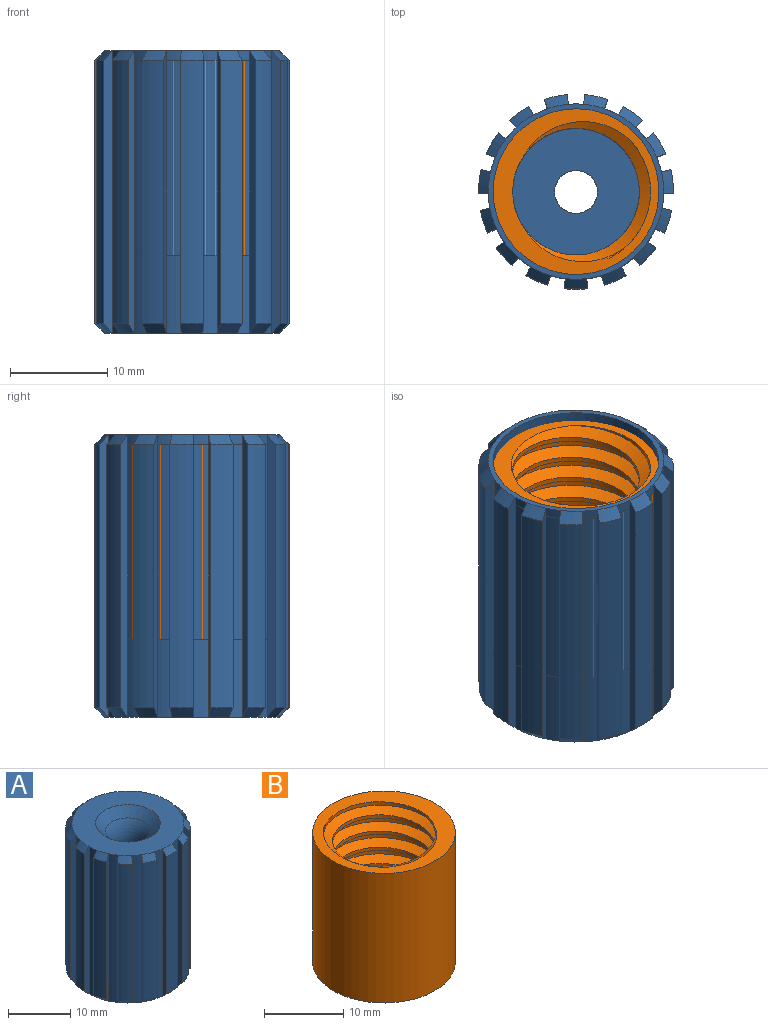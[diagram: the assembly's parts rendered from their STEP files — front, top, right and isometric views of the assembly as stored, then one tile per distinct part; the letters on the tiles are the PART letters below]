
ASSEMBLY  parts=2 mates=1
PART A: 97 faces, bbox 20x20x29 mm
  f0: cylinder r=10mm len=27mm, axis (0,0,-1), area 66mm2, adj f38,f62,f75,f84
  f1: cylinder r=10mm len=27mm, axis (0,0,-1), area 66mm2, adj f59,f64,f76,f83
  f2: cylinder r=10mm len=27mm, axis (0,0,-1), area 66mm2, adj f56,f61,f77,f82
  f3: cylinder r=10mm len=27mm, axis (0,0,-1), area 66mm2, adj f53,f58,f78,f81
  f4: cylinder r=10mm len=27mm, axis (0,0,-1), area 66mm2, adj f50,f55,f79,f80
  f5: cylinder r=10mm len=27mm, axis (0,0,-1), area 66mm2, adj f47,f52,f65,f94
  f6: cylinder r=10mm len=27mm, axis (0,0,-1), area 66mm2, adj f44,f49,f66,f93
  f7: cylinder r=10mm len=27mm, axis (0,0,-1), area 66mm2, adj f41,f46,f67,f92
  f8: cylinder r=10mm len=27mm, axis (0,0,-1), area 66mm2, adj f32,f39,f74,f85
  f9: cylinder r=10mm len=27mm, axis (0,0,-1), area 66mm2, adj f23,f36,f72,f87
  f10: cylinder r=10mm len=27mm, axis (0,0,-1), area 66mm2, adj f33,f35,f73,f86
  f11: cylinder r=10mm len=27mm, axis (0,0,-1), area 66mm2, adj f22,f30,f69,f90
  f12: cylinder r=10mm len=27mm, axis (0,0,-1), area 66mm2, adj f27,f29,f70,f89
  f13: cylinder r=10mm len=27mm, axis (0,0,-1), area 66mm2, adj f24,f26,f71,f88
  f14: plane 18x18mm, normal (0,0,1), area 169.5mm2, adj f21,f25,f28,f31,f34,f37,f40,f42
  f15: plane 18x18mm, normal (0,0,-1), area 27.5mm2, adj f19,f21,f25,f28,f31,f34,f37,f40
  f16: plane 17x17mm, normal (0,0,-1), area 211.8mm2, adj f18,f19
  f17: cylinder r=10mm len=27mm, axis (0,0,-1), area 66mm2, adj f20,f43,f68,f91
  f18: cylinder r=2.2mm len=4.4mm, axis (0,0,-1), area 40.5mm2, adj f16,f96
  f19: cylinder r=8.5mm len=21mm, axis (0,0,1), area 1121.5mm2, adj f15,f16
  f20: plane 29x1mm, normal (1,0.09,0), area 28mm2, adj f17,f21,f68,f91
  f21: cylinder r=9mm len=29mm, axis (0,0,1), area 45.6mm2, adj f14,f15,f20,f22
  f22: plane 29x1mm, normal (-1,0.09,0), area 28mm2, adj f11,f21,f69,f90
  f23: plane 29x0.97mm, normal (-0.22,0.97,0), area 28mm2, adj f9,f25,f72,f87
  f24: plane 29x0.92mm, normal (0.39,-0.92,0), area 28mm2, adj f13,f25,f71,f88
  f25: cylinder r=9mm len=29mm, axis (0,0,1), area 45.6mm2, adj f14,f15,f23,f24
  f26: plane 29x0.8mm, normal (-0.6,0.8,0), area 28mm2, adj f13,f28,f71,f88
  f27: plane 29x0.73mm, normal (0.73,-0.68,0), area 28mm2, adj f12,f28,f70,f89
  f28: cylinder r=9mm len=29mm, axis (0,0,1), area 45.6mm2, adj f14,f15,f26,f27
  f29: plane 29x0.87mm, normal (-0.87,0.48,0), area 28mm2, adj f12,f31,f70,f89
  f30: plane 29x0.95mm, normal (0.95,-0.33,0), area 28mm2, adj f11,f31,f69,f90
  f31: cylinder r=9mm len=29mm, axis (0,0,1), area 45.6mm2, adj f14,f15,f29,f30
  f32: plane 29x0.82mm, normal (0.57,0.82,0), area 28mm2, adj f8,f34,f74,f85
  f33: plane 29x0.91mm, normal (-0.42,-0.91,0), area 28mm2, adj f10,f34,f73,f86
  f34: cylinder r=9mm len=29mm, axis (0,0,1), area 45.6mm2, adj f14,f15,f32,f33
  f35: plane 29x0.98mm, normal (0.19,0.98,0), area 28mm2, adj f10,f37,f73,f86
  f36: plane 29x1mm, normal (-0.02,-1,0), area 28mm2, adj f9,f37,f72,f87
  f37: cylinder r=9mm len=29mm, axis (0,0,1), area 45.6mm2, adj f14,f15,f35,f36
  f38: plane 29x0.86mm, normal (0.86,0.52,0), area 28mm2, adj f0,f40,f75,f84
  f39: plane 29x0.75mm, normal (-0.75,-0.66,0), area 28mm2, adj f8,f40,f74,f85
  f40: cylinder r=9mm len=29mm, axis (0,0,1), area 45.6mm2, adj f14,f15,f38,f39
  f41: plane 29x0.87mm, normal (0.87,0.48,0), area 28mm2, adj f7,f42,f67,f92
  f42: cylinder r=9mm len=29mm, axis (0,0,1), area 45.6mm2, adj f14,f15,f41,f43
  f43: plane 29x0.95mm, normal (-0.95,-0.33,0), area 28mm2, adj f17,f42,f68,f91
  f44: plane 29x0.8mm, normal (0.6,0.8,0), area 28mm2, adj f6,f45,f66,f93
  f45: cylinder r=9mm len=29mm, axis (0,0,1), area 45.6mm2, adj f14,f15,f44,f46
  f46: plane 29x0.73mm, normal (-0.73,-0.68,0), area 28mm2, adj f7,f45,f67,f92
  f47: plane 29x0.97mm, normal (0.22,0.97,0), area 28mm2, adj f5,f48,f65,f94
  f48: cylinder r=9mm len=29mm, axis (0,0,1), area 45.6mm2, adj f14,f15,f47,f49
  f49: plane 29x0.92mm, normal (-0.39,-0.92,0), area 28mm2, adj f6,f48,f66,f93
  f50: plane 29x0.98mm, normal (-0.19,0.98,0), area 28mm2, adj f4,f51,f79,f80
  f51: cylinder r=9mm len=29mm, axis (0,0,1), area 45.6mm2, adj f14,f15,f50,f52
  f52: plane 29x1mm, normal (0.02,-1,0), area 28mm2, adj f5,f51,f65,f94
  f53: plane 29x0.82mm, normal (-0.57,0.82,0), area 28mm2, adj f3,f54,f78,f81
  f54: cylinder r=9mm len=29mm, axis (0,0,1), area 45.6mm2, adj f14,f15,f53,f55
  f55: plane 29x0.91mm, normal (0.42,-0.91,0), area 28mm2, adj f4,f54,f79,f80
  f56: plane 29x0.86mm, normal (-0.86,0.52,0), area 28mm2, adj f2,f57,f77,f82
  f57: cylinder r=9mm len=29mm, axis (0,0,1), area 45.6mm2, adj f14,f15,f56,f58
  f58: plane 29x0.75mm, normal (0.75,-0.66,0), area 28mm2, adj f3,f57,f78,f81
  f59: plane 29x0.99mm, normal (-0.99,0.12,0), area 28mm2, adj f1,f60,f76,f83
  f60: cylinder r=9mm len=29mm, axis (0,0,1), area 45.6mm2, adj f14,f15,f59,f61
  f61: plane 29x0.96mm, normal (0.96,-0.29,0), area 28mm2, adj f2,f60,f77,f82
  f62: plane 29x0.96mm, normal (-0.96,-0.29,0), area 28mm2, adj f0,f63,f75,f84
  f63: cylinder r=9mm len=29mm, axis (0,0,1), area 45.6mm2, adj f14,f15,f62,f64
  f64: plane 29x0.99mm, normal (0.99,0.12,0), area 28mm2, adj f1,f63,f76,f83
  f65: cone r=10mm half-angle=45deg, axis (0,0,1), area 3.3mm2, adj f5,f15,f47,f52
  f66: cone r=10mm half-angle=45deg, axis (0,0,1), area 3.3mm2, adj f6,f15,f44,f49
  f67: cone r=10mm half-angle=45deg, axis (0,0,1), area 3.3mm2, adj f7,f15,f41,f46
  f68: cone r=10mm half-angle=45deg, axis (0,0,1), area 3.3mm2, adj f15,f17,f20,f43
  f69: cone r=10mm half-angle=45deg, axis (0,0,1), area 3.3mm2, adj f11,f15,f22,f30
  f70: cone r=10mm half-angle=45deg, axis (0,0,1), area 3.3mm2, adj f12,f15,f27,f29
  f71: cone r=10mm half-angle=45deg, axis (0,0,1), area 3.3mm2, adj f13,f15,f24,f26
  f72: cone r=10mm half-angle=45deg, axis (0,0,1), area 3.3mm2, adj f9,f15,f23,f36
  f73: cone r=10mm half-angle=45deg, axis (0,0,1), area 3.3mm2, adj f10,f15,f33,f35
  f74: cone r=10mm half-angle=45deg, axis (0,0,1), area 3.3mm2, adj f8,f15,f32,f39
  f75: cone r=10mm half-angle=45deg, axis (0,0,1), area 3.3mm2, adj f0,f15,f38,f62
  f76: cone r=10mm half-angle=45deg, axis (0,0,1), area 3.3mm2, adj f1,f15,f59,f64
  f77: cone r=10mm half-angle=45deg, axis (0,0,1), area 3.3mm2, adj f2,f15,f56,f61
  f78: cone r=10mm half-angle=45deg, axis (0,0,1), area 3.3mm2, adj f3,f15,f53,f58
  f79: cone r=10mm half-angle=45deg, axis (0,0,1), area 3.3mm2, adj f4,f15,f50,f55
  f80: cone r=9mm half-angle=45deg, axis (0,0,-1), area 3.3mm2, adj f4,f14,f50,f55
  f81: cone r=9mm half-angle=45deg, axis (0,0,-1), area 3.3mm2, adj f3,f14,f53,f58
  f82: cone r=9mm half-angle=45deg, axis (0,0,-1), area 3.3mm2, adj f2,f14,f56,f61
  f83: cone r=9mm half-angle=45deg, axis (0,0,-1), area 3.3mm2, adj f1,f14,f59,f64
  f84: cone r=9mm half-angle=45deg, axis (0,0,-1), area 3.3mm2, adj f0,f14,f38,f62
  f85: cone r=9mm half-angle=45deg, axis (0,0,-1), area 3.3mm2, adj f8,f14,f32,f39
  f86: cone r=9mm half-angle=45deg, axis (0,0,-1), area 3.3mm2, adj f10,f14,f33,f35
  f87: cone r=9mm half-angle=45deg, axis (0,0,-1), area 3.3mm2, adj f9,f14,f23,f36
  f88: cone r=9mm half-angle=45deg, axis (0,0,-1), area 3.3mm2, adj f13,f14,f24,f26
  f89: cone r=9mm half-angle=45deg, axis (0,0,-1), area 3.3mm2, adj f12,f14,f27,f29
  f90: cone r=9mm half-angle=45deg, axis (0,0,-1), area 3.3mm2, adj f11,f14,f22,f30
  f91: cone r=9mm half-angle=45deg, axis (0,0,-1), area 3.3mm2, adj f14,f17,f20,f43
  f92: cone r=9mm half-angle=45deg, axis (0,0,-1), area 3.3mm2, adj f7,f14,f41,f46
  f93: cone r=9mm half-angle=45deg, axis (0,0,-1), area 3.3mm2, adj f6,f14,f44,f49
  f94: cone r=9mm half-angle=45deg, axis (0,0,-1), area 3.3mm2, adj f5,f14,f47,f52
  f95: cone r=2.2mm half-angle=45deg, axis (0,0,1), area 60.5mm2, adj f14,f96
  f96: torus R=7.2mm, axis (0,0,-1), area 66.6mm2, adj f18,f95
PART B: 7 faces, bbox 18.5x18.5x22.5 mm
  f0: cylinder r=9mm len=20mm, axis (0,0,-1), area 1131mm2, adj f4,f5
  f1: bspline ~21.91x17.67mm, area 472.6mm2, adj f2,f4,f5,f6
  f2: cylinder r=7.65mm len=20mm, axis (0,0,1), area 332.5mm2, adj f1,f3,f4,f5
  f3: bspline ~21.91x17.67mm, area 472mm2, adj f2,f4,f5,f6
  f4: plane 18.52x18.52mm, normal (0,0,1), area 94.8mm2, adj f0,f1,f2,f3,f6
  f5: plane 18.52x18.52mm, normal (0,0,-1), area 94.8mm2, adj f0,f1,f2,f3,f6
  f6: cylinder r=6.5mm len=20mm, axis (0,0,1), area 200.6mm2, adj f1,f3,f4,f5
PLACE A rot(axis=(0,1,0),180deg) t=(0,0,58)mm
PLACE B rot(axis=(0,-1,0),180deg) t=(0,0,30.5)mm
MATE fastened A.f19 <-> B.f0  axis (0,0,-1) through (0,0,8)mm
